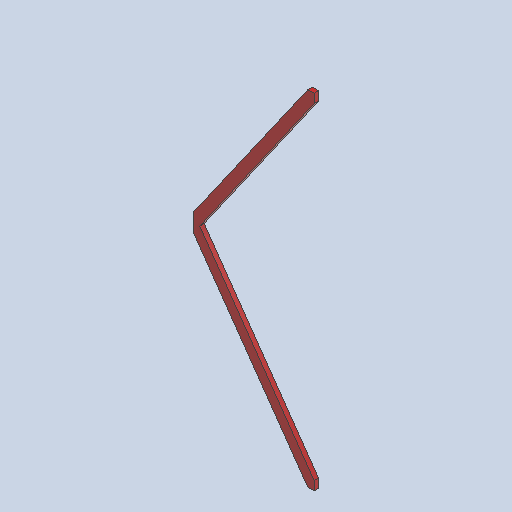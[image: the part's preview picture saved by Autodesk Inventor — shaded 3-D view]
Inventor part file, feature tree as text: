
AUTODESK INVENTOR PART (.ipt)
format: ipt  version: 2025 (Build 290162000, 162)  size: 267,776 bytes
history: native  units: in
note: dims shown in document units (in); Inventor stores cm internally (conversion verified against a paired STEP export)
features: other x7, reference x4, extrude x1, sketch x1
ambient origin geometry x8: Origin, YZ Plane, XZ Plane, XY Plane, X Axis, Y Axis, Z Axis, Center Point
bodies: Solid1 (feature_tree)
feature tree (13):
  extrude  "Extrusion1"  [1 undecoded]
  sketch  "Sketch1"  dims[d4=1.5in d5=0.0in]
  reference  "Reference1"
  reference  "Reference2"
  reference  "Reference3"
  reference  "Reference4"
  other  "<userpath>\Documents\USCTigerBurn24\Tburn24\F_Legs1\B_Legs0.iam"
  other  "B_Legs0.iam"
  other  "8'x2x4:3"
  other  "3'5x2x4:3"
  other  "8'x2x4:4"
  other  "3'5x2x4:2"
  other  "Finish1"
note: 1 required parameter value undecoded (feature->parameter linkage not recoverable at this tier; creation-order binding heuristic only, values carry confidence <= 0.55)
